# Revit family: BLAUBERG-KOMFORT_EC_LBE_400
name_source: partatom
category: Mechanical Equipment
units: mm (PartAtom-declared; Revit-internal decimal feet)

## family parameters
Always vertical = Yes
Classification = None
Cut with Voids When Loaded = No
OmniClass Number = 23.75.35.14
OmniClass Title = Air Handling Units
Part Type = Normal
Room Calculation Point = No
Round Connector Dimension = Use Diameter
Shared = No
Work Plane-Based = No

## types (2) — shared parameters
B = 682 mm  [stored 2.23753 ft]
B1 = 217 mm  [stored 0.711942 ft]
B2 = 217 mm  [stored 0.711942 ft]
BDrainCon = 341 mm  [stored 1.11877 ft]
Casing Material = Painted Steel White
CoverH = 247 mm
CoverH1 = 145 mm  [stored 0.475722 ft]
CoverL1 = 147 mm  [stored 0.482283 ft]
CoverL2 = 147 mm  [stored 0.482283 ft]
CoverW = 125 mm  [stored 0.410105 ft]
Current = 14 A
D = 200 mm  [stored 0.656168 ft]
Ddrain = 15 mm  [stored 0.0492126 ft]
Description = Air Handling Unit
Duct Connection Diameter = 200 mm  [stored 0.656168 ft]
ElBoxA = 159 mm  [stored 0.521654 ft]
ElBoxB = 364 mm  [stored 1.19423 ft]
ElConA = 249 mm  [stored 0.816929 ft]
ElConB = 341 mm  [stored 1.11877 ft]
Extract Air Filter = G4
Family Version = 1.0
Front Maintenance Zone Height = 900 mm  [stored 2.95276 ft]
H = 504 mm  [stored 1.65354 ft]
H1 = 141 mm
H2 = 162 mm  [stored 0.531496 ft]
HDrainCon = 52 mm
HDuctCon = 48 mm  [stored 0.15748 ft]
Heat Exchanger Type = counter-flow
Heater power = 2800 W
L = 1094 mm  [stored 3.58924 ft]
Load Classification = HVAC
Maintenance Zone Material = Maintenance Zone
Manufacturer = Blauberg
Maximum Air Flow = 540 m³/h
Maximum Unit Current With Electric Heater = 14 A
Maximum Unit Current Without Electric Heater = 2 A
Maximum Unit Power Without Electric Heater = 289 W
Metal Material = Metal Zinc
Number of Poles = 1
Plastic Material = Polypropylene Black
Power = 3089 W
Power Factor = 1
RPM (min-1) = 2600
Sound Pressure Level at 3 m (dBA) = 27
Supply Air Filter = G4+F7
Top Maintenance Zone Height = 900 mm  [stored 2.95276 ft]
Transported Air Temperature (°C) = -25…+40
URL = https://blaubergventilatoren.de
Voltage = 230 V
Weight = 76.00 kg
dBFeets = 58 mm  [stored 0.190289 ft]
dLFeets = 48 mm  [stored 0.15748 ft]

## per-type parameters (varying)
| type | Drain Connection Diameter | DrainPipe | Heat Exchanger Material | Heat recovery efficiency (%) | SEC Class | Type Comments |
| KOMFORT EC LBE 400 S21 | 16 mm  [stored 0.0524934 ft] | Yes | polystyrene | 84..98 | A+ | Air Handling Unit KOMFORT EC LBE 400 S21 |
| KOMFORT EC LBE 400-E S21 | 0 mm  [stored 0 ft] | No | enthalpy | 78..89 | A | Air Handling Unit KOMFORT EC LBE 400-E S21 |

note: column(s) folded — value = type name in every type: Model

note: [stored X ft] marks values corroborated as IEEE doubles in the binary element streams (Revit-internal decimal feet)

## geometry (parser evidence)
native form markers: Sweep x5
no freeform markers — native parametric forms only
